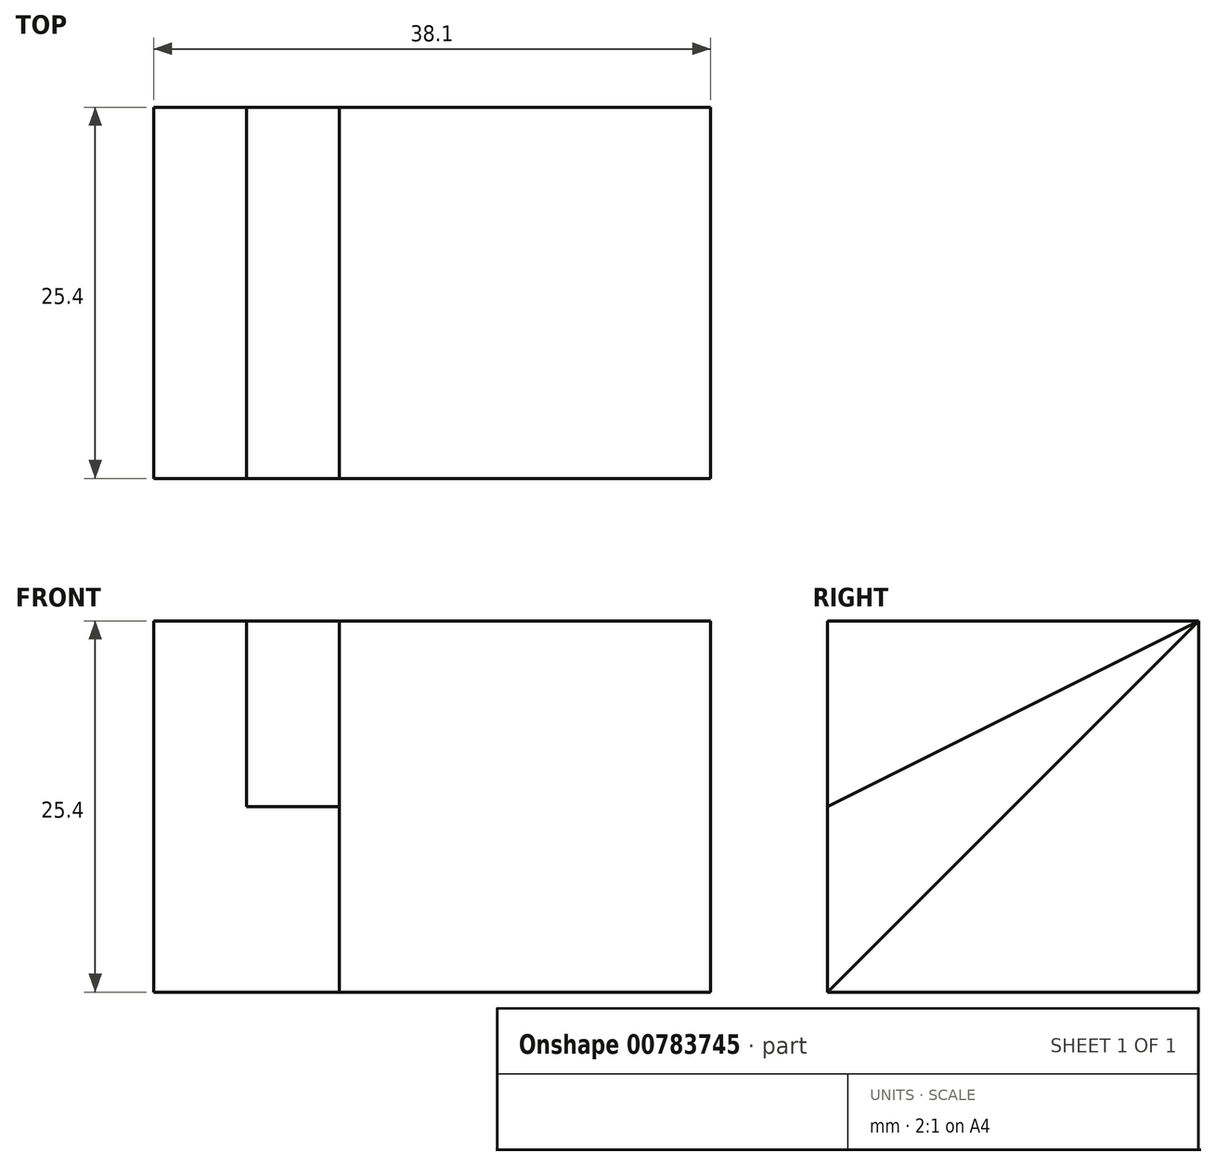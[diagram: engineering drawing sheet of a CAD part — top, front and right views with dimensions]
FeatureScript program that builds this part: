
annotation { "Feature Type Name" : "Feature", "Feature Type Description" : "" }
export const myFeature = defineFeature(function(context is Context, id is Id, definition is map)
    precondition{}
    {
        {
            var Q0;
            Q0=qCreatedBy(makeId("Front.planeOp"),FACE);
            var sketch = newSketch(context, id + "F0", { "sketchPlane" : qUnion([Q0])});
            skLineSegment(sketch, "E0", {"start": v(0, 0) * mm, "end": v(38.1, 0) * mm});
            skLineSegment(sketch, "E1", {"start": v(38.1, 0) * mm, "end": v(38.1, 25.4) * mm});
            skLineSegment(sketch, "E2", {"start": v(38.1, 25.4) * mm, "end": v(0, 25.4) * mm});
            skLineSegment(sketch, "E3", {"start": v(0, 25.4) * mm, "end": v(0, 0) * mm});
            skSolve(sketch);
        }
        {
            var Q0;
            Q0 = qSketchRegion(id + "F0", true);
            extrude(context, id + "F1", {"entities" : qUnion([Q0]), "depth" : 25.4 * mm, "offsetDistance" : 25.4 * mm});
        }
        {
            var Q0;
            Q0=makeQuery(id+"F1.opExtrude","SWEPT_FACE",FACE,{"disambiguationData":[OSD([sQuery(id+"F0.wireOp",EDGE,"E1")])]});
            var sketch = newSketch(context, id + "F2", { "sketchPlane" : qUnion([Q0])});
            skLineSegment(sketch, "E4", {"start": v(0, 25.4) * mm, "end": v(-25.4, 0) * mm});
            skSolve(sketch);
        }
        {
            var Q0;
            Q0 = qSketchRegion(id + "F2", true);
            var Q1;
            Q1=makeQuery(id+"F2.imprint","IMPRINT",FACE,{"disambiguationData":[TD([[makeQuery(id+"F2.imprint","IMPRINT",EDGE,{"derivedFrom":sQuery(id+"F2.wireOp",EDGE,"E4")}),-1.0]])]});
            extrude(context, id + "F3", {"entities" : qUnion([Q0, Q1]), "operationType" : NewBodyOperationType.REMOVE, "oppositeDirection" : true, "depth" : 25.4 * mm, "offsetDistance" : 25.4 * mm});
        }
        {
            var Q0;
            Q0=makeQuery(id+"F3.boolean.opBoolean","COPY",FACE,{"derivedFrom":makeQuery(id+"F3.opExtrude","CAP_FACE",FACE,{"disambiguationData":[OSD([sQuery(id+"F0.wireOp",EDGE,"E1"),sQuery(id+"F0.wireOp",EDGE,"E2"),sQuery(id+"F2.wireOp",EDGE,"E4")])],"isStart":false})});
            var sketch = newSketch(context, id + "F4", { "sketchPlane" : qUnion([Q0])});
            skLineSegment(sketch, "E5", {"start": v(0, 25.4) * mm, "end": v(-25.4, 12.7) * mm});
            skSolve(sketch);
        }
        {
            var Q0;
            Q0 = qSketchRegion(id + "F4", true);
            var Q1;
            {var subQ0=sQuery(id+"F4.wireOp",EDGE,"E5");Q1=makeQuery(id+"F4.imprint","IMPRINT",FACE,{"disambiguationData":[TD([[makeQuery(id+"F4.imprint","IMPRINT",EDGE,{"derivedFrom":subQ0}),-1.0]])]});}
            extrude(context, id + "F5", {"entities" : qUnion([Q0, Q1]), "operationType" : NewBodyOperationType.REMOVE, "oppositeDirection" : true, "depth" : 6.35 * mm, "offsetDistance" : 25.4 * mm});
        }
    });
